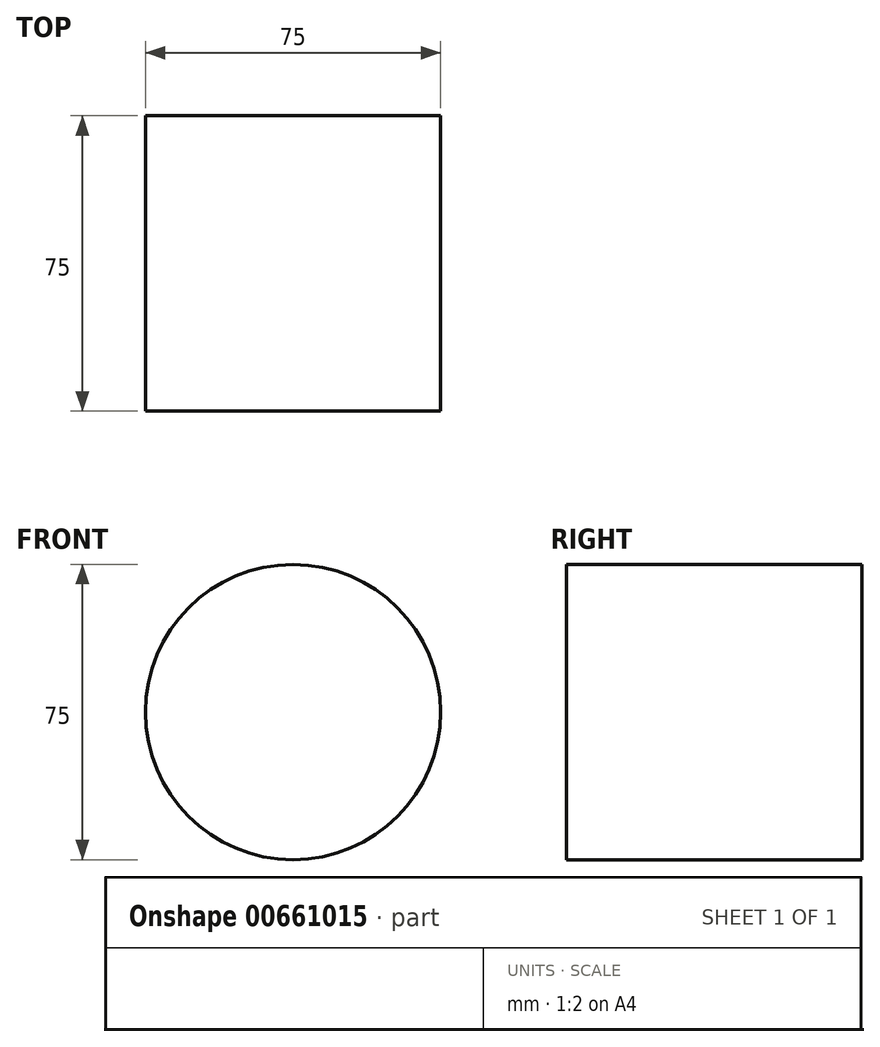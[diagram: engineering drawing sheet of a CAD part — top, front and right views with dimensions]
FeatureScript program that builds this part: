
annotation { "Feature Type Name" : "Feature", "Feature Type Description" : "" }
export const myFeature = defineFeature(function(context is Context, id is Id, definition is map)
    precondition{}
    {
        {
            var Q0;
            Q0=qCreatedBy(makeId("Front.planeOp"),FACE);
            var sketch = newSketch(context, id + "F0", { "sketchPlane" : qUnion([Q0])});
            skCircle(sketch, "E0", {"center": v(0, 0) * mm, "radius": 37.5 * mm});
            skSolve(sketch);
        }
        {
            var Q0;
            Q0=makeQuery(id+"F0.imprint","IMPRINT",FACE,{"disambiguationData":[TD([[makeQuery(id+"F0.imprint","IMPRINT",EDGE,{"derivedFrom":sQuery(id+"F0.wireOp",EDGE,"E0")}),1.0]])]});
            extrude(context, id + "F1", {"entities" : qUnion([Q0]), "endBound" : BoundingType.SYMMETRIC, "depth" : 75 * mm, "offsetDistance" : 25 * mm});
        }
    });
